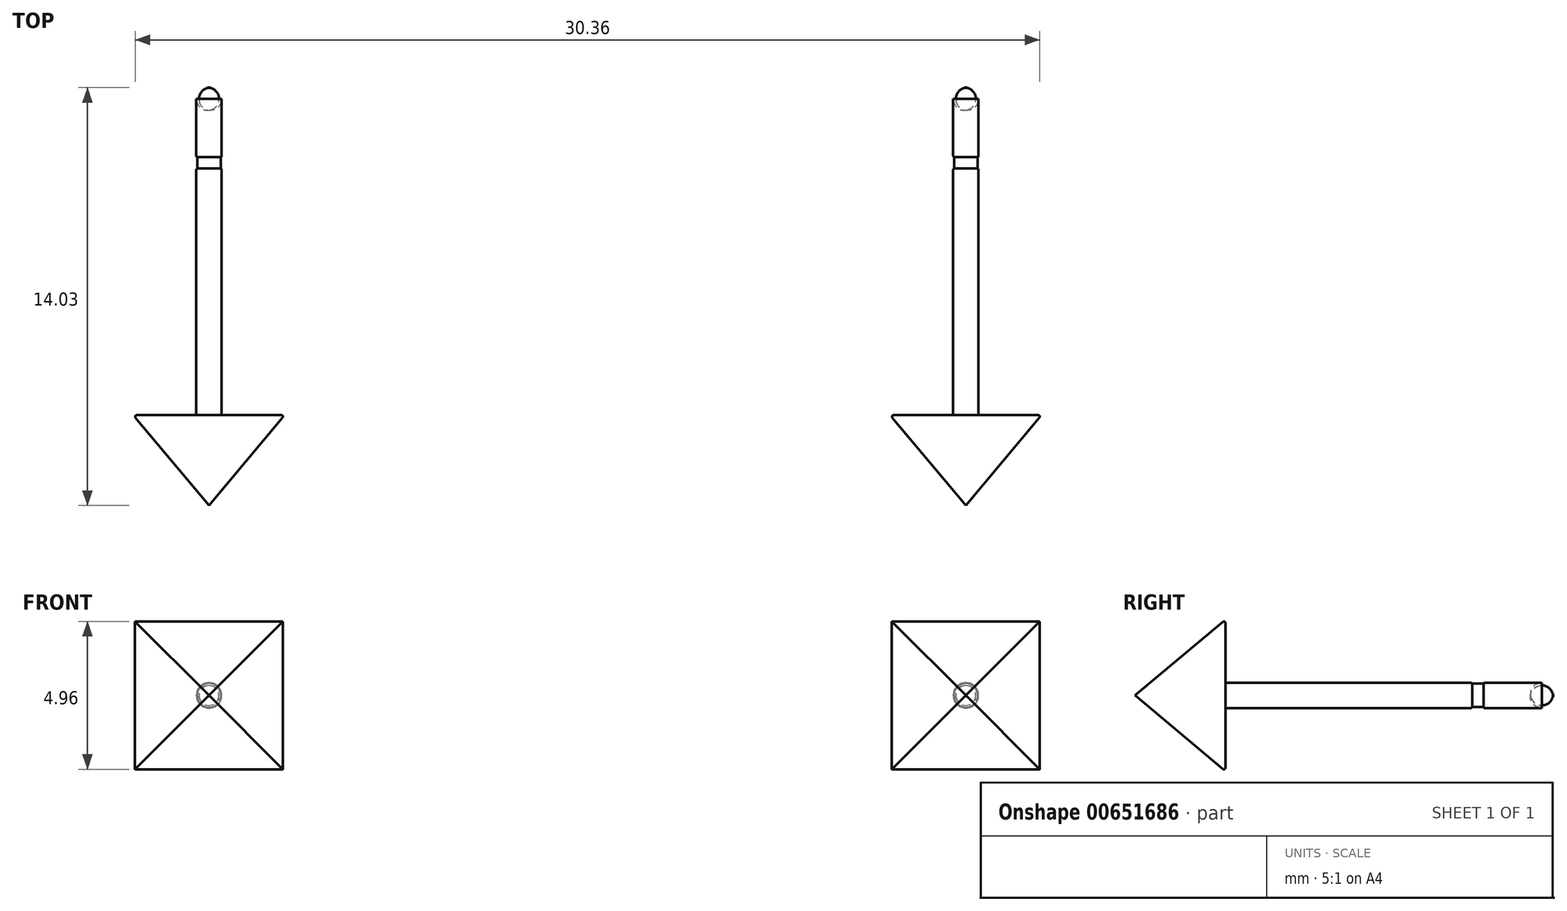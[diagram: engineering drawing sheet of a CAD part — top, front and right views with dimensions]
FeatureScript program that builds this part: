
annotation { "Feature Type Name" : "Feature", "Feature Type Description" : "" }
export const myFeature = defineFeature(function(context is Context, id is Id, definition is map)
    precondition{}
    {
        {
            var Q0;
            Q0=qCreatedBy(makeId("Front.planeOp"),FACE);
            var sketch = newSketch(context, id + "F0", { "sketchPlane" : qUnion([Q0])});
            skLineSegment(sketch, "E0.bottom", {"start": v(10.16, 5.08) * mm, "end": v(15.24, 5.08) * mm});
            skLineSegment(sketch, "E0.top", {"start": v(10.16, 0) * mm, "end": v(15.24, 0) * mm});
            skLineSegment(sketch, "E0.left", {"start": v(10.16, 5.08) * mm, "end": v(10.16, 0) * mm});
            skLineSegment(sketch, "E0.right", {"start": v(15.24, 5.08) * mm, "end": v(15.24, 0) * mm});
            skSolve(sketch);
        }
        {
            var Q0;
            Q0=makeQuery(id+"F0.imprint","IMPRINT",FACE,{"disambiguationData":[TD([[makeQuery(id+"F0.imprint","IMPRINT",EDGE,{"derivedFrom":sQuery(id+"F0.wireOp",EDGE,"E0.bottom")}),-1.0]])]});
            extrude(context, id + "F1", {"entities" : qUnion([Q0]), "depth" : 5.08 * mm, "offsetDistance" : 25.4 * mm, "hasDraft" : true, "draftAngle" : 40 * degree, "draftPullDirection" : true});
        }
        {
            var Q0;
            Q0=qCreatedBy(makeId("Front.planeOp"),FACE);
            var sketch = newSketch(context, id + "F2", { "sketchPlane" : qUnion([Q0])});
            skCircle(sketch, "E1", {"center": v(12.7, 2.54) * mm, "radius": 0.42 * mm});
            skSolve(sketch);
        }
        {
            var Q0;
            Q0 = qSketchRegion(id + "F2", true);
            extrude(context, id + "F3", {"entities" : qUnion([Q0]), "operationType" : NewBodyOperationType.ADD, "oppositeDirection" : true, "depth" : 11 * mm, "offsetDistance" : 25.4 * mm});
        }
        {
            var Q0;
            Q0=makeQuery(id+"F3.opExtrude","CAP_EDGE",EDGE,{"disambiguationData":[OSD([sQuery(id+"F2.wireOp",EDGE,"E1")])],"isStart":false});
            fillet(context, id + "F4", {"entities" : qUnion([Q0]), "radius" : 0.38 * mm, "tangentPropagation" : true, "allowEdgeOverflow" : false});
        }
        {
            var Q0;
            Q0=makeQuery(id+"F1.opExtrude","CAP_EDGE",EDGE,{"disambiguationData":[OSD([sQuery(id+"F0.wireOp",EDGE,"E0.right")])],"isStart":true});
            var Q1;
            Q1=makeQuery(id+"F1.opExtrude","CAP_EDGE",EDGE,{"disambiguationData":[OSD([sQuery(id+"F0.wireOp",EDGE,"E0.bottom")])],"isStart":true});
            var Q2;
            Q2=makeQuery(id+"F1.opExtrude","CAP_EDGE",EDGE,{"disambiguationData":[OSD([sQuery(id+"F0.wireOp",EDGE,"E0.left")])],"isStart":true});
            var Q3;
            Q3=makeQuery(id+"F1.opExtrude","CAP_EDGE",EDGE,{"disambiguationData":[OSD([sQuery(id+"F0.wireOp",EDGE,"E0.top")])],"isStart":true});
            fillet(context, id + "F5", {"entities" : qUnion([Q0, Q1, Q2, Q3]), "radius" : 0.05 * mm, "tangentPropagation" : true, "allowEdgeOverflow" : false});
        }
        {
            var Q0;
            Q0=qCreatedBy(makeId("Right.planeOp"),FACE);
            cPlane(context, id + "F6", {"entities" : qUnion([Q0]), "cplaneType" : CPlaneType.OFFSET, "offset" : 12.7 * mm, "width" : 152.4 * mm, "height" : 152.4 * mm});
        }
        {
            var Q0;
            Q0=qCreatedBy(id+"F6.planeOp",FACE);
            var sketch = newSketch(context, id + "F7", { "sketchPlane" : qUnion([Q0])});
            skLineSegment(sketch, "E2.bottom", {"start": v(8.28, 3.1) * mm, "end": v(8.66, 3.1) * mm});
            skLineSegment(sketch, "E2.top", {"start": v(8.28, 2.93) * mm, "end": v(8.66, 2.93) * mm});
            skLineSegment(sketch, "E2.left", {"start": v(8.28, 3.1) * mm, "end": v(8.28, 2.93) * mm});
            skLineSegment(sketch, "E2.right", {"start": v(8.66, 3.1) * mm, "end": v(8.66, 2.93) * mm});
            skLineSegment(sketch, "E3", {"start": v(6.47, 2.54) * mm, "end": v(11.9, 2.54) * mm, "construction": true});
            skPoint(sketch, "E4", {"position": v(10.62, 2.54) * mm});
            skSolve(sketch);
        }
        {
            var Q0;
            Q0=makeQuery(id+"F7.imprint","IMPRINT",FACE,{"disambiguationData":[TD([[makeQuery(id+"F7.imprint","IMPRINT",EDGE,{"derivedFrom":sQuery(id+"F7.wireOp",EDGE,"E2.bottom")}),-1.0]])]});
            var Q1;
            Q1=sQuery(id+"F7.wireOp",EDGE,"E3");
            revolve(context, id + "F8", {"operationType" : NewBodyOperationType.REMOVE, "entities" : qUnion([Q0]), "axis" : qUnion([Q1]), "revolveType" : RevolveType.FULL, "oppositeDirection" : true});
        }
        {
            var Q0;
            Q0=makeQuery(id+"F8.boolean.opBoolean","INTERSECT",EDGE,{"derivedFrom":[makeQuery(id+"F3.opExtrude","SWEPT_FACE",FACE,{"disambiguationData":[OSD([sQuery(id+"F2.wireOp",EDGE,"E1")])]}),makeQuery(id+"F8.opRevolve","SWEPT_FACE",FACE,{"disambiguationData":[OSD([sQuery(id+"F7.wireOp",EDGE,"E2.left")])]})]});
            var Q1;
            Q1=makeQuery(id+"F8.boolean.opBoolean","INTERSECT",EDGE,{"derivedFrom":[makeQuery(id+"F3.opExtrude","SWEPT_FACE",FACE,{"disambiguationData":[OSD([sQuery(id+"F2.wireOp",EDGE,"E1")])]}),makeQuery(id+"F8.opRevolve","SWEPT_FACE",FACE,{"disambiguationData":[OSD([sQuery(id+"F7.wireOp",EDGE,"E2.right")])]})]});
            fillet(context, id + "F9", {"entities" : qUnion([Q0, Q1]), "radius" : 0.05 * mm, "tangentPropagation" : true, "allowEdgeOverflow" : false});
        }
        {
            var Q0;
            Q0=makeQuery(id+"F1.opExtrude","SWEPT_BODY",BODY,{"disambiguationData":[OSD([sQuery(id+"F0.wireOp",EDGE,"E0.bottom"),sQuery(id+"F0.wireOp",EDGE,"E0.top"),sQuery(id+"F0.wireOp",EDGE,"E0.left"),sQuery(id+"F0.wireOp",EDGE,"E0.right")])]});
            var Q1;
            Q1=qCreatedBy(makeId("Right.planeOp"),FACE);
            mirror(context, id + "F10", {"entities" : qUnion([Q0]), "mirrorPlane" : qUnion([Q1])});
        }
    });
